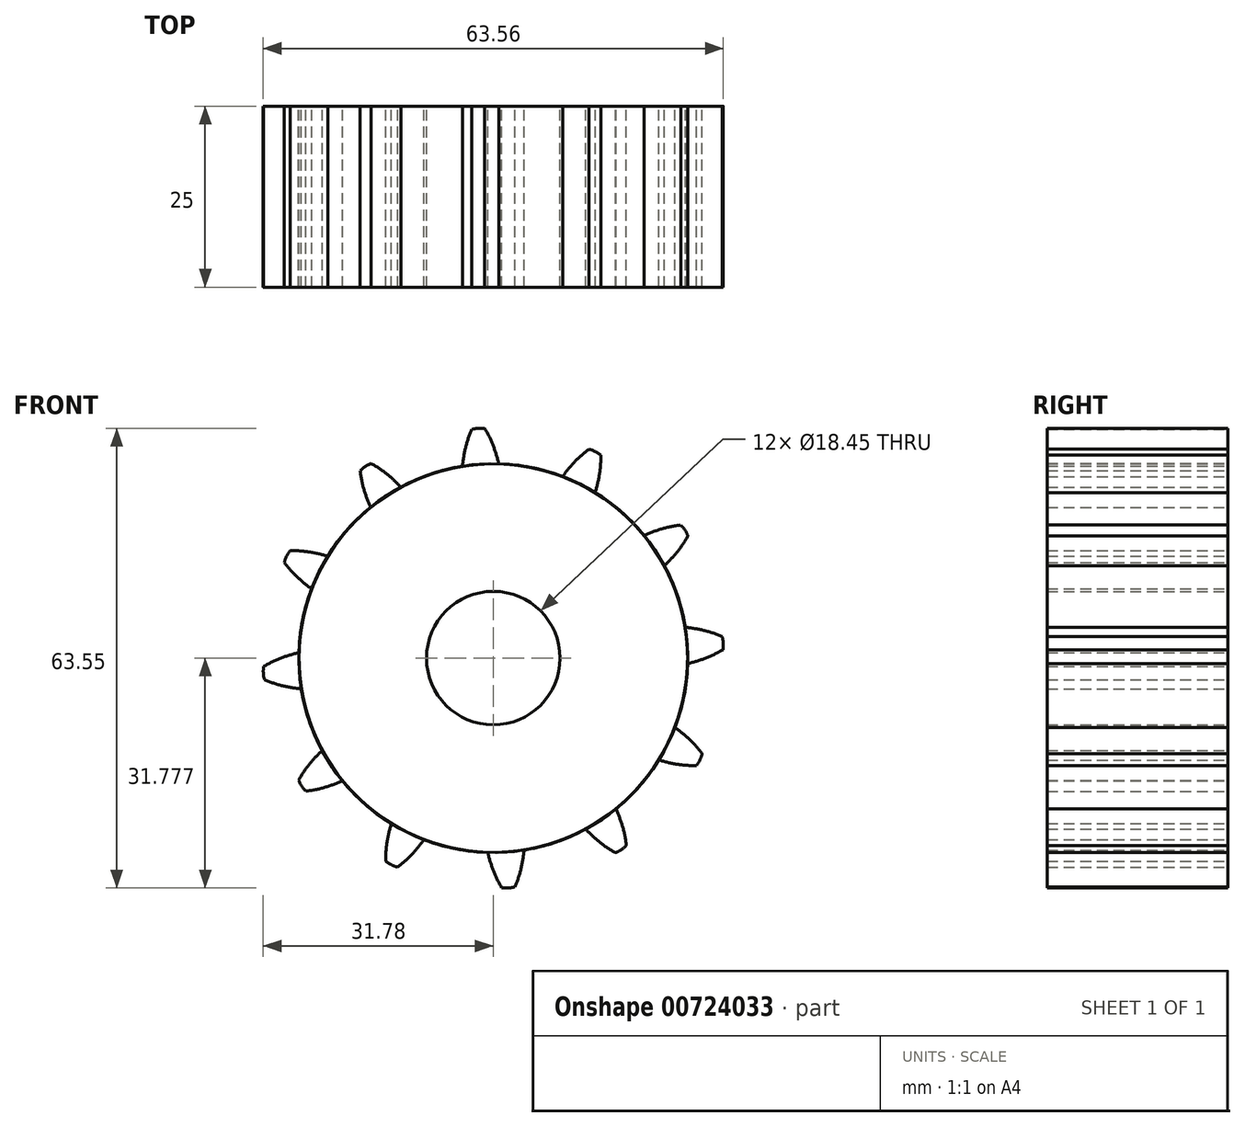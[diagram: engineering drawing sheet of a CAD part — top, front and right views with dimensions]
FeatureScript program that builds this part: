
annotation { "Feature Type Name" : "Feature", "Feature Type Description" : "" }
export const myFeature = defineFeature(function(context is Context, id is Id, definition is map)
    precondition{}
    {
        {
            var Q0;
            Q0=qCreatedBy(makeId("Front.planeOp"),FACE);
            var sketch = newSketch(context, id + "F0", { "sketchPlane" : qUnion([Q0])});
            skCircle(sketch, "E0", {"center": v(5.88, 1.06) * mm, "radius": 26.86 * mm});
            skCircle(sketch, "E1", {"center": v(5.88, 1.06) * mm, "radius": 29.34 * mm, "construction": true});
            skCircle(sketch, "E2", {"center": v(5.88, 1.06) * mm, "radius": 31.75 * mm, "construction": true});
            skLineSegment(sketch, "E3", {"start": v(5.88, 1.06) * mm, "end": v(5.88, 63.56) * mm, "construction": true});
            skLineSegment(sketch, "E4", {"start": v(5.88, 1.06) * mm, "end": v(-1.53, 114.15) * mm, "construction": true});
            skLineSegment(sketch, "E5", {"start": v(5.88, 30.4) * mm, "end": v(-77.62, 28.3) * mm, "construction": true});
            skLineSegment(sketch, "E6", {"start": v(5.88, 30.4) * mm, "end": v(-69.5, 0.8) * mm, "construction": true});
            skCircle(sketch, "E7", {"center": v(5.88, 1.06) * mm, "radius": 27.3 * mm, "construction": true});
            skCircle(sketch, "E8", {"center": v(5.88, 30.4) * mm, "radius": 16.52 * mm, "construction": true});
            skCircle(sketch, "E9", {"center": v(-9.5, 24.36) * mm, "radius": 16.52 * mm, "construction": true});
            skArc(sketch, "E10", {"start": v(5.88, 30.4) * mm, "mid": v(5.35, 31.62) * mm, "end": v(4.71, 32.79) * mm});
            skArc(sketch, "E11", {"start": v(6.64, 27.9) * mm, "mid": v(6.3, 29.16) * mm, "end": v(5.88, 30.4) * mm});
            skArc(sketch, "E12.MirrorCS", {"start": v(1.63, 27.58) * mm, "mid": v(1.8, 28.87) * mm, "end": v(2.05, 30.14) * mm});
            skArc(sketch, "E13.MirrorCS", {"start": v(2.05, 30.14) * mm, "mid": v(2.42, 31.42) * mm, "end": v(2.9, 32.67) * mm});
            skArc(sketch, "E14", {"start": v(4.71, 32.79) * mm, "mid": v(3.8, 32.82) * mm, "end": v(2.9, 32.67) * mm});
            skCircle(sketch, "E15", {"center": v(5.88, 1.06) * mm, "radius": 9.23 * mm});
            skSolve(sketch);
        }
        {
            var Q0;
            Q0=makeQuery(id+"F0.imprint","IMPRINT",FACE,{"disambiguationData":[TD([[makeQuery(id+"F0.imprint","IMPRINT",EDGE,{"derivedFrom":sQuery(id+"F0.wireOp",EDGE,"E15")}),-1.0]])]});
            var Q1;
            Q1=makeQuery(id+"F0.imprint","IMPRINT",FACE,{"disambiguationData":[TD([[makeQuery(id+"F0.imprint","IMPRINT",EDGE,{"derivedFrom":sQuery(id+"F0.wireOp",EDGE,"E10")}),1.0]])]});
            extrude(context, id + "F1", {"entities" : qUnion([Q0, Q1]), "depth" : 25 * mm, "offsetDistance" : 25 * mm});
        }
        {
            var Q0;
            Q0=makeQuery(id+"F1.opExtrude","SWEPT_BODY",BODY,{"disambiguationData":[OSD([sQuery(id+"F0.wireOp",EDGE,"E0"),sQuery(id+"F0.wireOp",EDGE,"E10"),sQuery(id+"F0.wireOp",EDGE,"E11"),sQuery(id+"F0.wireOp",EDGE,"E12.MirrorCS"),sQuery(id+"F0.wireOp",EDGE,"E13.MirrorCS"),sQuery(id+"F0.wireOp",EDGE,"E14"),sQuery(id+"F0.wireOp",EDGE,"d7CvMHU0-aT7p-n7wz-PCfX-v61lBfdPXALf"),sQuery(id+"F0.wireOp",EDGE,"uzpvFnsd-GnE0-4gXE-lHBN-rzUIRUwnZdSH"),sQuery(id+"F0.wireOp",EDGE,"MUtpbA0o-Qlic-Yfms-SiW6-Jp7doFPjTLDG"),sQuery(id+"F0.wireOp",EDGE,"NMHNrnj3-fi6a-ucIZ-fh8S-flCCPQwexdwp"),sQuery(id+"F0.wireOp",EDGE,"N453Tnoa-UpVe-J9Li-RgFl-N6vw9Q7D3wNZ"),sQuery(id+"F0.wireOp",EDGE,"vEuPz1eb-RC3o-6GOh-enzg-4keSjtaC7SoS"),sQuery(id+"F0.wireOp",EDGE,"bc40ltv4-grGC-bkLu-FoLL-5pfnlnU9LsQu")])]});
            var Q1;
            Q1=makeQuery(id+"F1.opExtrude","SWEPT_FACE",FACE,{"disambiguationData":[OSD([sQuery(id+"F0.wireOp",EDGE,"E0")])]});
            circularPattern(context, id + "F2", {"entities" : qUnion([Q0]), "axis" : qUnion([Q1]), "angle" : 360 * degree, "instanceCount" : 12, "equalSpace" : true});
        }
    });
